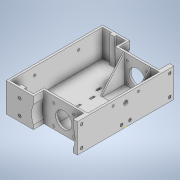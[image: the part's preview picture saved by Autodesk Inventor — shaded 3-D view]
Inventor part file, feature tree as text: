
AUTODESK INVENTOR PART (.ipt)
format: ipt  version: 2020 (Build 240168000, 168)  size: 413,184 bytes
history: native  units: mm
features: sketch x16, extrude x8, hole x5, plane x2, mirror x2, rib x1
ambient origin geometry x8: Origin, YZ Plane, XZ Plane, XY Plane, X Axis, Y Axis, Z Axis, Center Point
bodies: Solid1 (feature_tree)
feature tree (34):
  sketch  "Sketch1"  dims[d0=115.0mm d1=170.0mm]
  sketch  "Sketch2"  dims[d2=65.0mm d3=95.0mm]
  sketch  "Sketch3"  dims[d4=25.0mm d5=90.0mm]
  extrude  "Extrusion1"  Depth=170.0mm
  extrude  "Extrusion2"  Depth=95.0mm
  extrude  "Extrusion3"  Depth=90.0mm
  extrude  "Extrusion4"  Depth=30.0mm
  plane  "Work Plane1"
  rib  "Rib1"
  plane  "Work Plane2"
  mirror  "Mirror1"
  extrude  "Extrusion6"  Depth=5.0mm
  extrude  "Extrusion8"  Depth=60.0mm
  hole  "Hole1"  [1 undecoded]
  sketch  "Sketch10"  dims[d23=0.0mm d24=0.0mm d25=0.0mm]
  hole  "Hole2"  [1 undecoded]
  hole  "Hole4"  [1 undecoded]
  extrude  "Extrusion9"  TaperAngle=0.0deg  [1 undecoded]
  hole  "Hole6"  [1 undecoded]
  extrude  "Extrusion10"  Depth=10.0mm TaperAngle=0.0deg
  mirror  "Mirror2"
  hole  "Hole5"  [1 undecoded]
  sketch  "Sketch4"  dims[d7=72.0mm d8=30.0mm]
  sketch  "Sketch5"  dims[d9=5.0mm d10=0.0mm d12=5.0mm]
  sketch  "Sketch6"  dims[d13=64.0mm d14=0.0mm d15=60.0mm]
  sketch  "Sketch7"  dims[d16=55.0mm d17=3.0mm d18=0.0mm]
  sketch  "Sketch8"  dims[d19=47.14mm d20=29.0mm]
  sketch  "Sketch9"  dims[d21=5.2mm d22=39.0mm]
  sketch  "Sketch12"  dims[d26=1.0mm d27=3.0mm d28=0.0mm d29=0.0mm d30=1.0mm d31=1.0mm d32=47.14mm]
  sketch  "Sketch13"  dims[d33=104.0mm d36=10.0mm d37=0.0mm]
  sketch  "Sketch14"  dims[d38=52.5mm d40=51.0mm]
  sketch  "Sketch15"  dims[d41=5.2mm d42=6.0mm d43=4.0mm d44=2.0mm d45=90.0deg d46=8.0mm d47=0.0mm]
  sketch  "Sketch16"  dims[d48=10.0mm]
  sketch  "Sketch17"  dims[d49=10.0mm d50=5.9mm d51=6.0mm d52=6.5mm d53=2.0mm d54=90.0deg d55=8.5mm d56=0.0mm d57=10.0mm d58=10.0mm d64=20.0mm d65=8.0mm d66=20.0mm d67=0.0mm d68=10.0mm d69=10.0mm d77=10.0mm d78=30.0mm d79=5.2mm d80=6.0mm d81=4.0mm d82=2.0mm d83=90.0deg d84=8.5mm d85=0.0mm d86=51.0mm d87=5.2mm d88=6.0mm d89=10.0mm d90=2.5mm d91=90.0deg d92=5.0mm d93=0.0mm d94=5.0mm d95=12.0mm d96=21.5mm d97=64.0mm d98=0.0mm d99=32.5mm d100=12.5mm d101=5.9mm d102=6.0mm d103=6.5mm d104=2.5mm d105=90.0deg d106=8.5mm d107=0.0mm d108=20.0mm d109=2.0mm d110=4.0mm d111=2.0mm d112=4.0mm d113=2.0mm d114=4.0mm d115=64.0mm d116=0.0mm d117=10.0mm d118=25.0mm d119=25.0mm d120=10.0mm]
note: 6 required parameter values undecoded (feature->parameter linkage not recoverable at this tier; creation-order binding heuristic only, values carry confidence <= 0.55)
